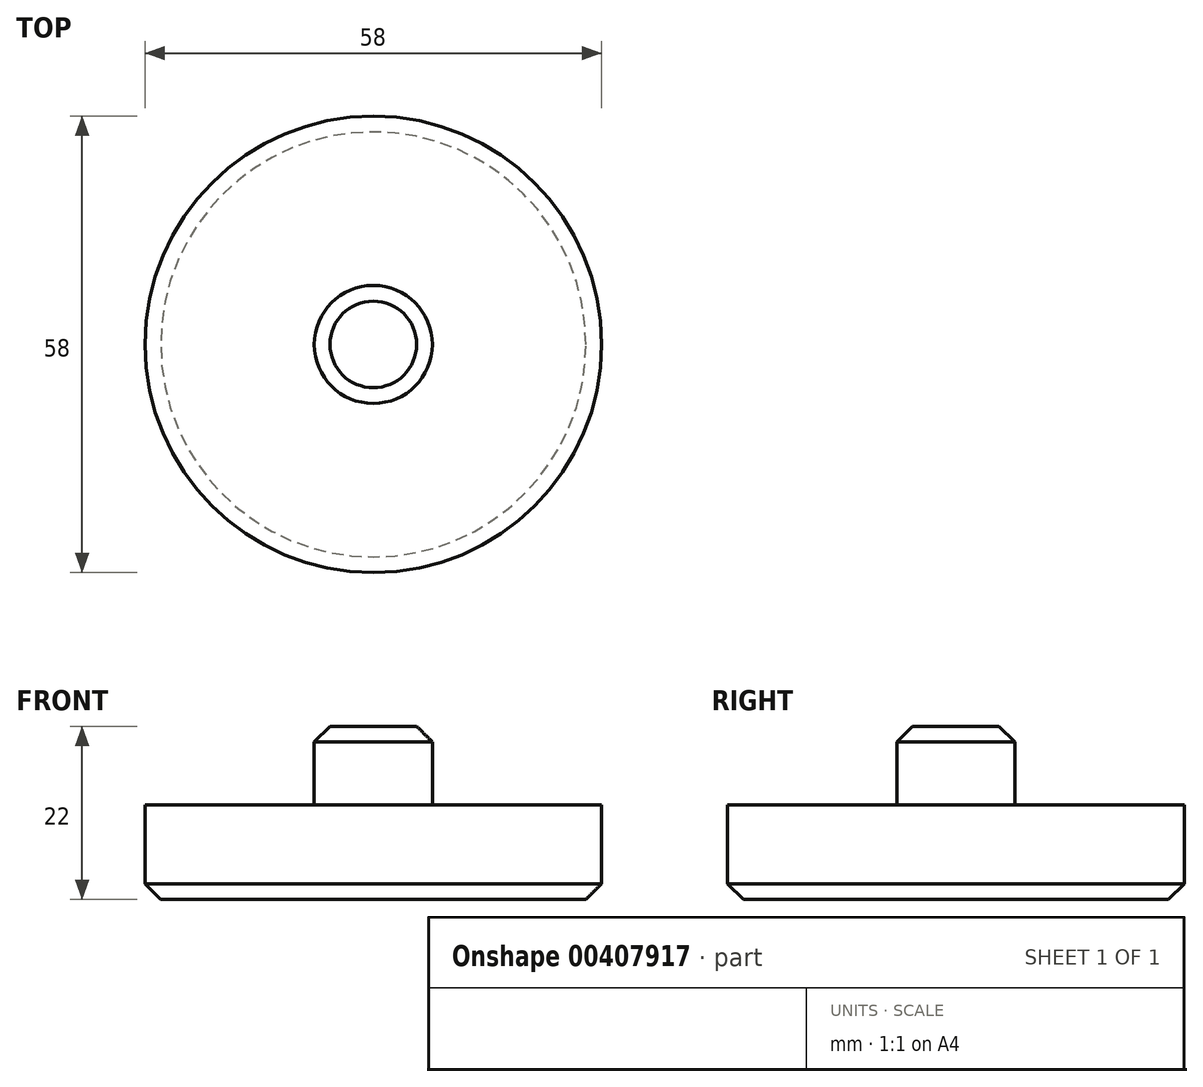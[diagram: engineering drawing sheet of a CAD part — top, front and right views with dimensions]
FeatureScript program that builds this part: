
annotation { "Feature Type Name" : "Feature", "Feature Type Description" : "" }
export const myFeature = defineFeature(function(context is Context, id is Id, definition is map)
    precondition{}
    {
        {
            var Q0;
            Q0=qCreatedBy(makeId("Top.planeOp"),FACE);
            var sketch = newSketch(context, id + "F0", { "sketchPlane" : qUnion([Q0])});
            skCircle(sketch, "E0", {"center": v(0, 0) * mm, "radius": 29 * mm});
            skSolve(sketch);
        }
        {
            var Q0;
            Q0 = qSketchRegion(id + "F0", true);
            extrude(context, id + "F1", {"entities" : qUnion([Q0]), "depth" : 12 * mm});
        }
        {
            var Q0;
            Q0=makeQuery(id+"F1.opExtrude","CAP_FACE",FACE,{"disambiguationData":[OSD([sQuery(id+"F0.wireOp",EDGE,"E0")])],"isStart":false});
            var sketch = newSketch(context, id + "F2", { "sketchPlane" : qUnion([Q0])});
            skCircle(sketch, "E1", {"center": v(0, 0) * mm, "radius": 7.5 * mm});
            skSolve(sketch);
        }
        {
            var Q0;
            Q0 = qSketchRegion(id + "F2", true);
            extrude(context, id + "F3", {"entities" : qUnion([Q0]), "operationType" : NewBodyOperationType.ADD, "depth" : 10 * mm});
        }
        {
            var Q0;
            Q0=makeQuery(id+"F3.opExtrude","CAP_EDGE",EDGE,{"disambiguationData":[OSD([sQuery(id+"F2.wireOp",EDGE,"E1")])],"isStart":false});
            chamfer(context, id + "F4", {"entities" : qUnion([Q0]), "width" : 2 * mm, "tangentPropagation" : true});
        }
        {
            var Q0;
            Q0=makeQuery(id+"F1.opExtrude","CAP_EDGE",EDGE,{"disambiguationData":[OSD([sQuery(id+"F0.wireOp",EDGE,"E0")])],"isStart":true});
            chamfer(context, id + "F5", {"entities" : qUnion([Q0]), "width" : 2 * mm, "tangentPropagation" : true});
        }
    });
